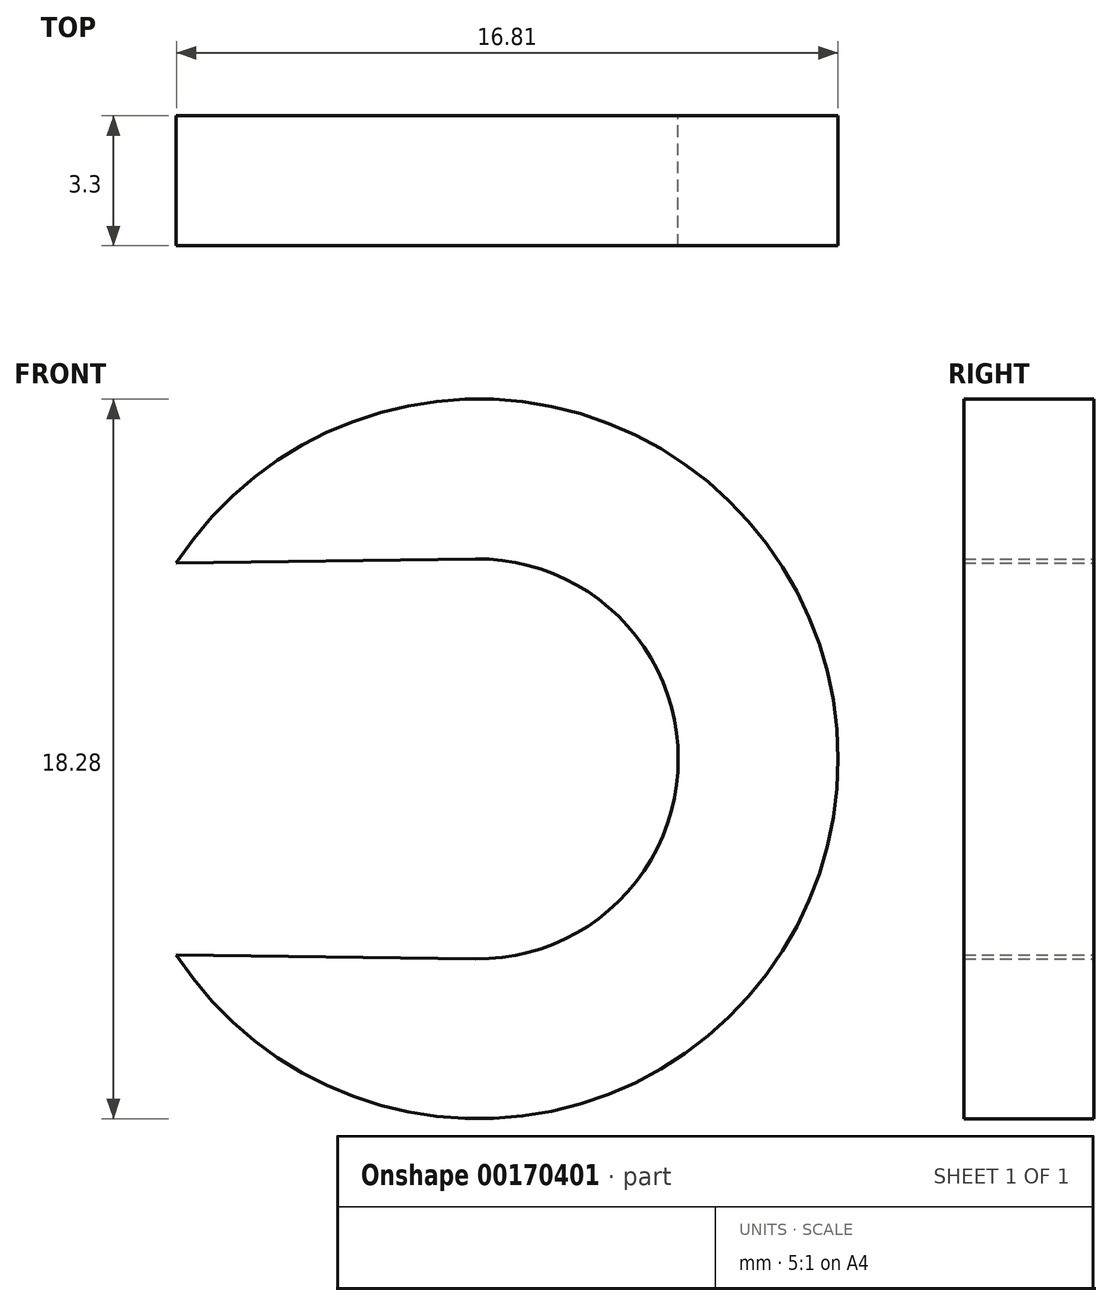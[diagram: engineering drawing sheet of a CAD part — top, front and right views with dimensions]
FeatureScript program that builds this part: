
annotation { "Feature Type Name" : "Feature", "Feature Type Description" : "" }
export const myFeature = defineFeature(function(context is Context, id is Id, definition is map)
    precondition{}
    {
        {
            var Q0;
            Q0=qCreatedBy(makeId("Front.planeOp"),FACE);
            var sketch = newSketch(context, id + "F0", { "sketchPlane" : qUnion([Q0])});
            skArc(sketch, "E0", {"start": v(-0.07, -5.08) * mm, "mid": v(5.08, 0) * mm, "end": v(-0.07, 5.08) * mm});
            skArc(sketch, "E1", {"start": v(-7.67, -4.97) * mm, "mid": v(9.14, 0) * mm, "end": v(-7.67, 4.97) * mm});
            skLineSegment(sketch, "E2", {"start": v(-9.14, 0) * mm, "end": v(-9.14, 4.95) * mm, "construction": true});
            skLineSegment(sketch, "E3", {"start": v(-9.14, 0) * mm, "end": v(-9.14, -4.95) * mm, "construction": true});
            skLineSegment(sketch, "E4", {"start": v(-7.67, 4.97) * mm, "end": v(0, 5.08) * mm});
            skLineSegment(sketch, "E5", {"start": v(-7.67, -4.97) * mm, "end": v(0, -5.08) * mm});
            skSolve(sketch);
        }
        {
            var Q0;
            Q0 = qSketchRegion(id + "F0", true);
            extrude(context, id + "F1", {"entities" : qUnion([Q0]), "depth" : 3.3 * mm});
        }
    });
